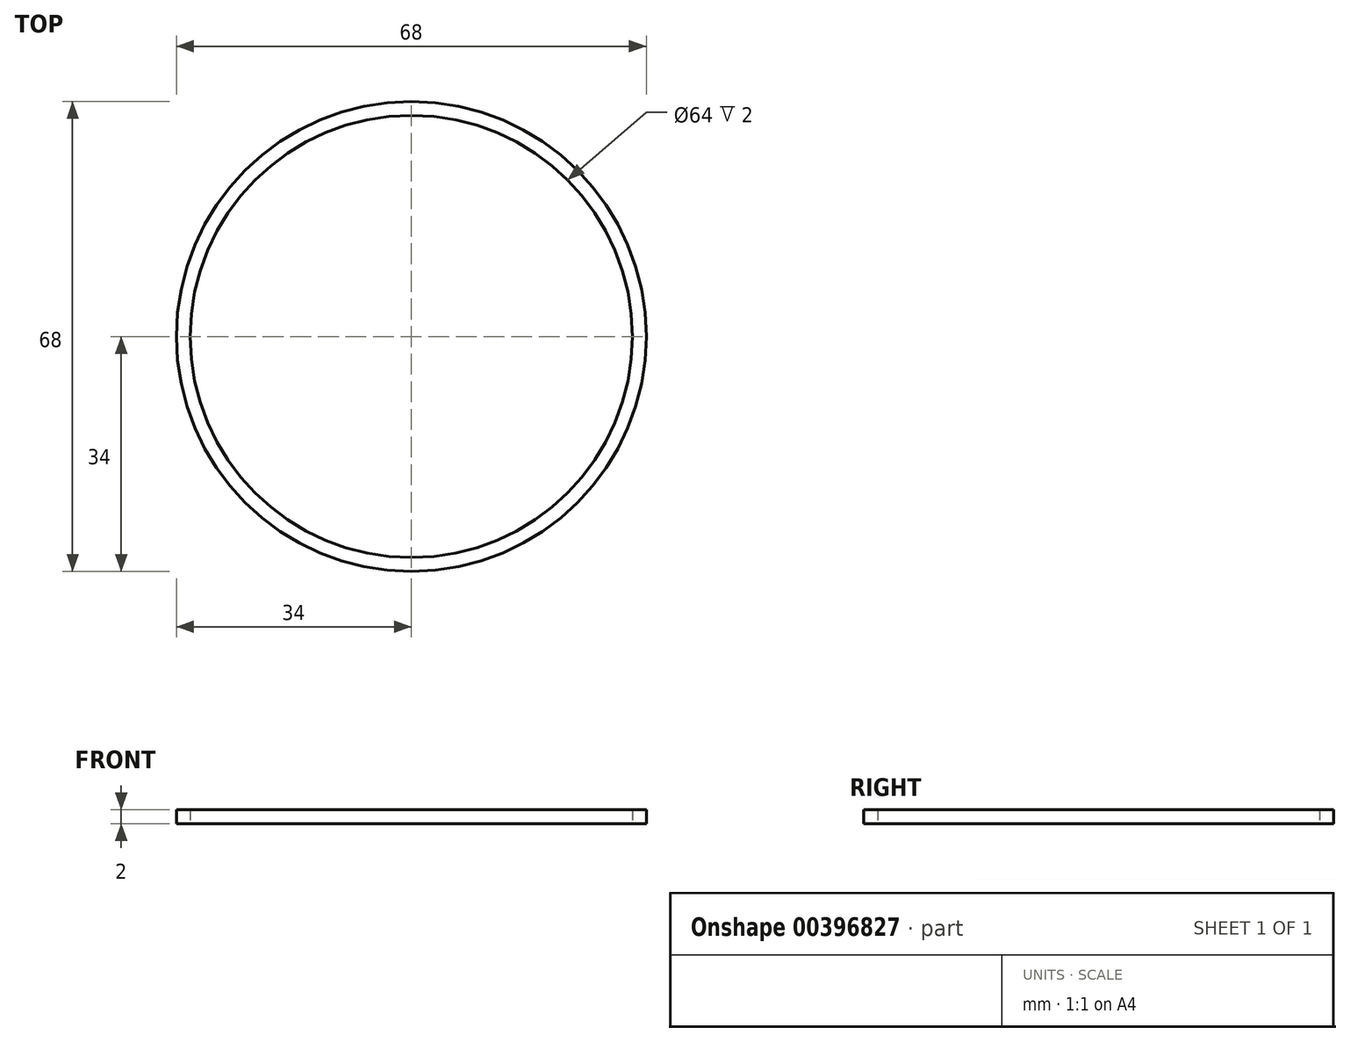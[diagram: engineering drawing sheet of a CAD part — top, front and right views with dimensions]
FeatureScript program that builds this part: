
annotation { "Feature Type Name" : "Feature", "Feature Type Description" : "" }
export const myFeature = defineFeature(function(context is Context, id is Id, definition is map)
    precondition{}
    {
        {
            var Q0;
            Q0=qCreatedBy(makeId("Top.planeOp"),FACE);
            var sketch = newSketch(context, id + "F0", { "sketchPlane" : qUnion([Q0])});
            skCircle(sketch, "E0", {"center": v(0, 0) * mm, "radius": 32 * mm});
            skCircle(sketch, "E1", {"center": v(0, 0) * mm, "radius": 34 * mm});
            skSolve(sketch);
        }
        {
            var Q0;
            Q0=makeQuery(id+"F0.imprint","IMPRINT",FACE,{"disambiguationData":[TD([[makeQuery(id+"F0.imprint","IMPRINT",EDGE,{"derivedFrom":sQuery(id+"F0.wireOp",EDGE,"E0")}),-1.0]])]});
            extrude(context, id + "F1", {"entities" : qUnion([Q0]), "depth" : 2 * mm});
        }
    });
